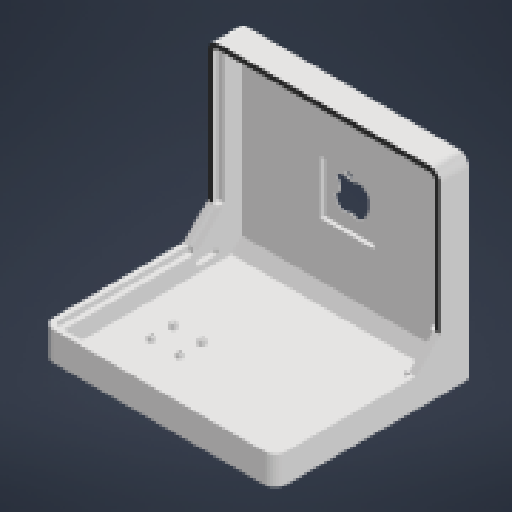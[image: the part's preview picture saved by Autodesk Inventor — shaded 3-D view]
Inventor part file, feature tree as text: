
AUTODESK INVENTOR PART (.ipt)
format: ipt  version: 2024.2 (Build 282272000, 272)  size: 901,120 bytes
history: native  units: mm
features: projected_geometry x20, extrude x15, sketch x15, other x5, reference x3, chamfer x2, fillet x1, shell x1
ambient origin geometry x8: Origin, YZ Plane, XZ Plane, XY Plane, X Axis, Y Axis, Z Axis, Center Point
bodies: Body1 (feature_tree), Body2 (feature_tree)
feature tree (62):
  other  "솔리드1"
  extrude  "돌출1"  Depth=217.0mm
  extrude  "돌출7"  Depth=131.0mm
  extrude  "돌출8"  Depth=27.0mm TaperAngle=0.0deg
  fillet  "모깎기5"  Radius=50.0mm
  chamfer  "모따기3"  Distance=27.0mm
  shell  "쉘3"  Thickness=154.0mm
  extrude  "돌출11"  Depth=10.0mm
  extrude  "돌출12"  Depth=23.0mm TaperAngle=45.0deg
  chamfer  "모따기4"  Distance=10.0mm
  extrude  "돌출13"  Depth=5.0mm TaperAngle=0.0deg
  extrude  "돌출14"  Depth=5.0mm TaperAngle=0.0deg
  extrude  "돌출15"  Depth=10.0mm TaperAngle=45.0deg
  extrude  "돌출16"  Depth=50.0mm
  extrude  "돌출17"  Depth=50.0mm
  extrude  "돌출18"  Depth=197.0mm
  extrude  "돌출19"  Depth=156.0mm
  extrude  "돌출20"  Depth=98.5mm
  extrude  "돌출21"  Depth=181.0mm
  extrude  "돌출22"  Depth=90.5mm
  sketch  "스케치1"
  sketch  "스케치8"
  projected_geometry  "투영된 루프3"
  sketch  "스케치9"
  sketch  "스케치12"
  projected_geometry  "투영된 루프6"
  sketch  "스케치13"
  projected_geometry  "투영된 루프7"
  sketch  "스케치15"
  projected_geometry  "투영된 루프8"
  projected_geometry  "투영된 루프9"
  sketch  "스케치17"
  projected_geometry  "투영된 루프11"
  sketch  "스케치21"
  projected_geometry  "투영된 루프14"
  sketch  "스케치22"
  projected_geometry  "투영된 루프15"
  sketch  "스케치23"
  projected_geometry  "투영된 루프16"
  projected_geometry  "투영된 루프17"
  sketch  "스케치24"
  projected_geometry  "투영된 루프18"
  reference  "참조1"
  sketch  "스케치25"
  reference  "참조2"
  projected_geometry  "투영된 루프19"
  projected_geometry  "투영된 루프20"
  sketch  "스케치27"
  projected_geometry  "투영된 루프21"
  projected_geometry  "투영된 루프22"
  projected_geometry  "투영된 루프23"
  projected_geometry  "투영된 루프24"
  sketch  "스케치28"
  projected_geometry  "투영된 루프25"
  reference  "참조3"
  sketch  "스케치29"
  projected_geometry  "투영된 루프26"
  projected_geometry  "투영된 루프27"
  other  "<userpath>\OneDrive\AAST\PART\AAST Remote Controler\AASTRC case.iam"
  other  "AASTRC case.iam"
  other  "AASTRC Middle case cover assembly:1"
  other  "AASTRC Middle case cover:1"
